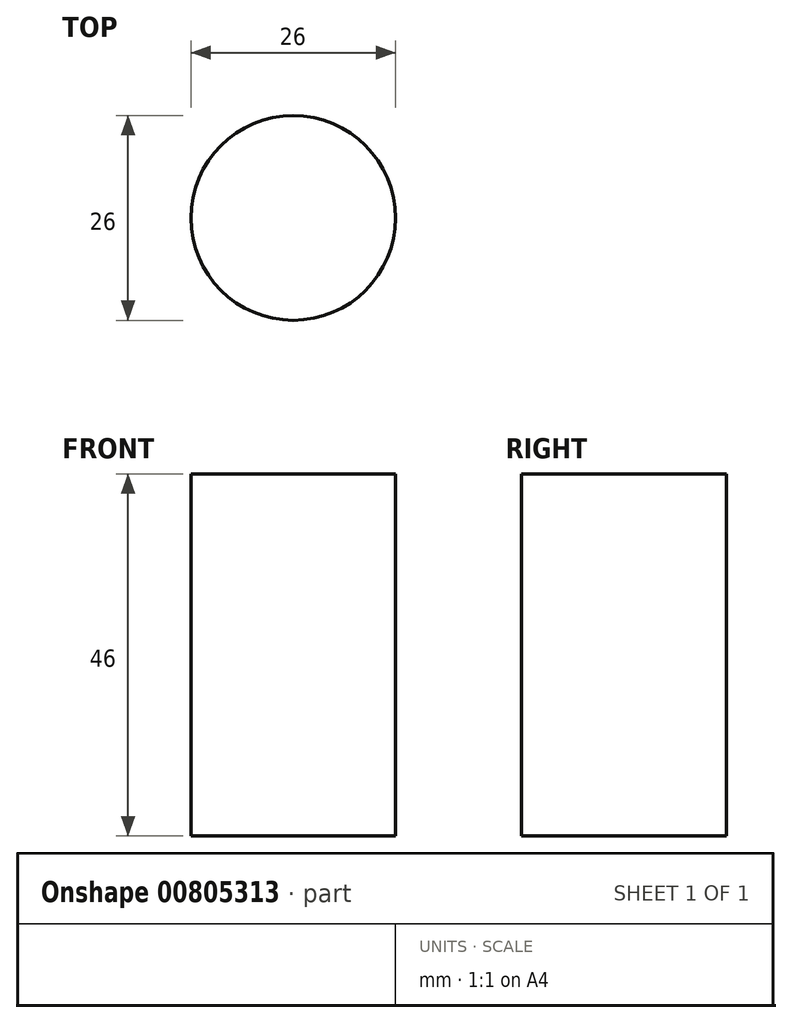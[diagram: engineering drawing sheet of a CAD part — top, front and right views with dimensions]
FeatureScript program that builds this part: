
annotation { "Feature Type Name" : "Feature", "Feature Type Description" : "" }
export const myFeature = defineFeature(function(context is Context, id is Id, definition is map)
    precondition{}
    {
        {
            var Q0;
            Q0=qCreatedBy(makeId("Top.planeOp"),FACE);
            var sketch = newSketch(context, id + "F0", { "sketchPlane" : qUnion([Q0])});
            skCircle(sketch, "E0", {"center": v(0, 0) * mm, "radius": 13 * mm});
            skSolve(sketch);
        }
        {
            var Q0;
            Q0 = qSketchRegion(id + "F0", true);
            extrude(context, id + "F1", {"entities" : qUnion([Q0]), "depth" : 46 * mm, "offsetDistance" : 25 * mm});
        }
    });
